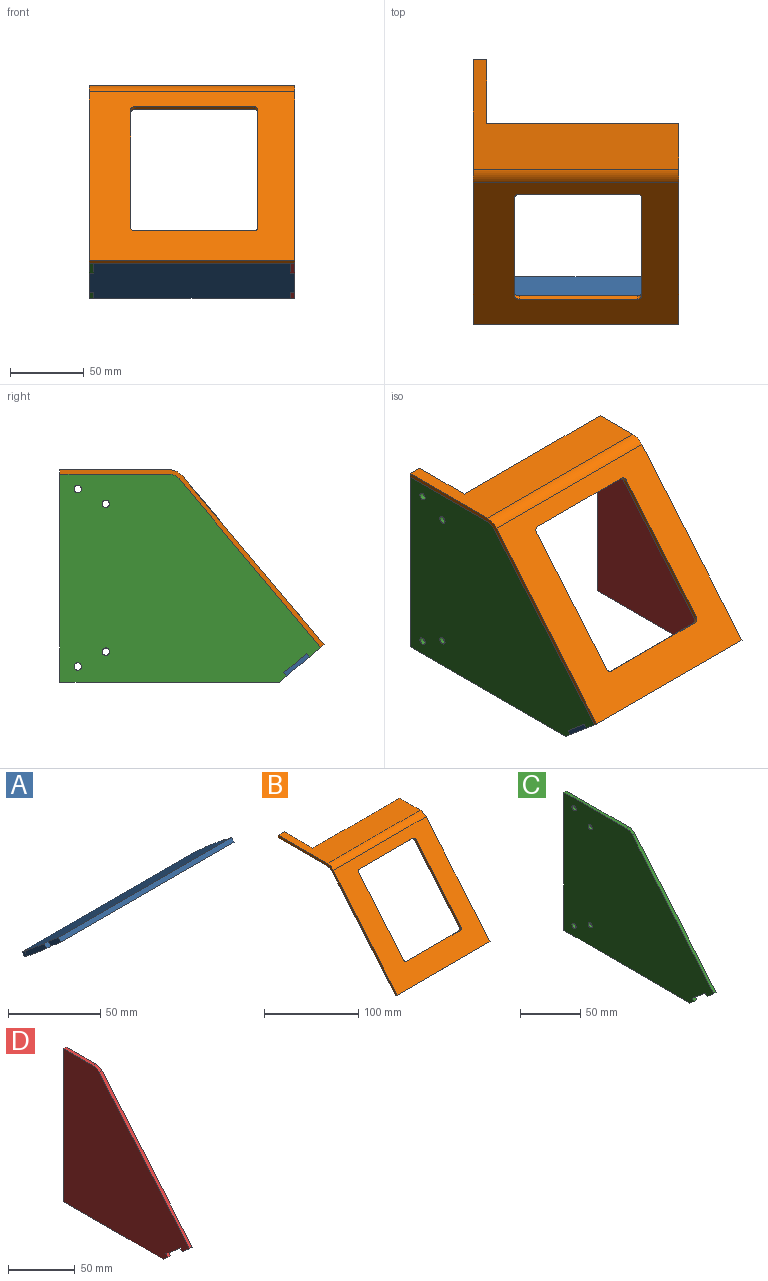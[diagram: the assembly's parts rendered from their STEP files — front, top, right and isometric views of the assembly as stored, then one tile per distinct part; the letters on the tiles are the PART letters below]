
ASSEMBLY  parts=4 mates=3
PART A: 14 faces, bbox 139x29.7x25.6 mm
  f0: plane 17.25x15.15mm, normal (1,0,0), area 60mm2, adj f1,f11,f12,f13
  f1: plane 3x2.3mm, normal (0,-0.77,0.64), area 9mm2, adj f0,f2,f12,f13
  f2: plane 9.59x8.73mm, normal (1,0,0), area 30mm2, adj f1,f3,f12,f13
  f3: plane 133x2.3mm, normal (0,-0.77,0.64), area 399mm2, adj f2,f4,f12,f13
  f4: plane 9.59x8.73mm, normal (-1,0,0), area 30mm2, adj f3,f5,f12,f13
  f5: plane 3x2.3mm, normal (0,-0.77,0.64), area 9mm2, adj f4,f6,f12,f13
  f6: plane 17.25x15.15mm, normal (-1,0,0), area 60mm2, adj f5,f7,f12,f13
  f7: plane 3x2.3mm, normal (0,0.77,-0.64), area 9mm2, adj f6,f8,f12,f13
  f8: plane 6.75x6.35mm, normal (-1,0,0), area 18.9mm2, adj f7,f9,f12,f13
  f9: plane 133x2.3mm, normal (0,0.77,-0.64), area 399mm2, adj f8,f10,f12,f13
  f10: plane 6.75x6.35mm, normal (1,0,0), area 18.9mm2, adj f9,f11,f12,f13
  f11: plane 3x2.3mm, normal (0,0.77,-0.64), area 9mm2, adj f0,f10,f12,f13
  f12: plane 139x27.81mm, normal (0,0.64,0.77), area 4947.9mm2, adj f0,f1,f2,f3,f4,f5,f6,f7
  f13: plane 139x27.81mm, normal (0,-0.64,-0.77), area 4947.9mm2, adj f0,f1,f2,f3,f4,f5,f6,f7
PART B: 20 faces, bbox 139x178.6x120.2 mm
  f0: plane 130x3mm, normal (0,1,0), area 390mm2, adj f5,f6,f9,f19
  f1: plane 139x114.14mm, normal (0,0.77,-0.64), area 11259.2mm2, adj f3,f4,f8,f9,f10,f11,f12,f13
  f2: plane 139x114.14mm, normal (0,-0.77,0.64), area 11259.2mm2, adj f3,f7,f8,f9,f10,f11,f12,f13
  f3: plane 139x2.3mm, normal (0,-0.64,-0.77), area 417mm2, adj f1,f2,f8,f9
  f4: cylinder r=8.57mm len=139mm, axis (1,0,0), area 1039.5mm2, adj f1,f5,f8,f9
  f5: plane 139x74mm, normal (0,0,-1), area 4696.5mm2, adj f0,f4,f8,f9,f18,f19
  f6: plane 139x74mm, normal (0,0,1), area 4696.5mm2, adj f0,f7,f8,f9,f18,f19
  f7: cylinder r=11.57mm len=139mm, axis (1,0,0), area 1403.4mm2, adj f2,f6,f8,f9
  f8: plane 178.64x120.21mm, normal (-1,0,0), area 695.4mm2, adj f1,f2,f3,f4,f5,f6,f7,f18
  f9: plane 135.64x120.21mm, normal (1,0,0), area 566.4mm2, adj f0,f1,f2,f3,f4,f5,f6,f7
  f10: plane 81.6x69.15mm, normal (-1,0,0), area 312mm2, adj f1,f2,f11,f17
  f11: cylinder r=3mm len=4.23mm, axis (0,-0.77,0.64), area 14.1mm2, adj f1,f2,f10,f12
  f12: plane 80x2.3mm, normal (0,-0.64,-0.77), area 240mm2, adj f1,f2,f11,f13
  f13: cylinder r=3mm len=4.23mm, axis (0,-0.77,0.64), area 14.1mm2, adj f1,f2,f12,f14
  f14: plane 81.6x69.15mm, normal (1,0,0), area 312mm2, adj f1,f2,f13,f15
  f15: cylinder r=3mm len=4.23mm, axis (0,-0.77,0.64), area 14.1mm2, adj f1,f2,f14,f16
  f16: plane 80x2.3mm, normal (0,0.64,0.77), area 240mm2, adj f1,f2,f15,f17
  f17: cylinder r=3mm len=4.23mm, axis (0,-0.77,0.64), area 14.1mm2, adj f1,f2,f10,f16
  f18: plane 9x3mm, normal (0,1,0), area 27mm2, adj f5,f6,f8,f19
  f19: plane 43x3mm, normal (1,0,0), area 129mm2, adj f0,f5,f6,f18
PART C: 16 faces, bbox 3x176.3x140.6 mm
  f0: plane 74x3mm, normal (0,0,1), area 222mm2, adj f1,f12,f14,f15
  f1: cylinder r=8.57mm len=6.57mm, axis (-1,0,0), area 22.4mm2, adj f0,f2,f14,f15
  f2: plane 114.14x95.78mm, normal (0,-0.77,0.64), area 447mm2, adj f1,f3,f14,f15
  f3: plane 7.66x6.43mm, normal (0,-0.64,-0.77), area 30mm2, adj f2,f4,f14,f15
  f4: plane 3x2.3mm, normal (0,0.77,-0.64), area 9mm2, adj f3,f5,f14,f15
  f5: plane 15.32x12.86mm, normal (0,-0.64,-0.77), area 60mm2, adj f4,f6,f14,f15
  f6: plane 3x2.3mm, normal (0,-0.77,0.64), area 9mm2, adj f5,f7,f14,f15
  f7: plane 4.92x4.13mm, normal (0,-0.64,-0.77), area 19.3mm2, adj f6,f8,f14,f15
  f8: plane 148.44x3mm, normal (0,0,-1), area 445.3mm2, adj f7,f12,f14,f15
  f9: cylinder r=2.5mm len=5mm, axis (-1,0,0), area 47.1mm2, adj f14,f15
  f10: cylinder r=2.5mm len=5mm, axis (-1,0,0), area 47.1mm2, adj f14,f15
  f11: cylinder r=2.5mm len=5mm, axis (-1,0,0), area 47.1mm2, adj f14,f15
  f12: plane 140.62x3mm, normal (0,1,0), area 421.9mm2, adj f0,f8,f14,f15
  f13: cylinder r=2.5mm len=5mm, axis (-1,0,0), area 47.1mm2, adj f14,f15
  f14: plane 176.35x140.62mm, normal (1,0,0), area 18566.8mm2, adj f0,f1,f2,f3,f4,f5,f6,f7
  f15: plane 176.35x140.62mm, normal (-1,0,0), area 18566.8mm2, adj f0,f1,f2,f3,f4,f5,f6,f7
PART D: 12 faces, bbox 3x133.3x140.6 mm
  f0: plane 140.62x3mm, normal (0,1,0), area 421.9mm2, adj f1,f9,f10,f11
  f1: plane 31x3mm, normal (0,0,1), area 93mm2, adj f0,f2,f10,f11
  f2: cylinder r=8.57mm len=6.57mm, axis (1,0,0), area 22.4mm2, adj f1,f3,f10,f11
  f3: plane 114.14x95.78mm, normal (0,-0.77,0.64), area 447mm2, adj f2,f4,f10,f11
  f4: plane 7.66x6.43mm, normal (0,-0.64,-0.77), area 30mm2, adj f3,f5,f10,f11
  f5: plane 3x2.3mm, normal (0,0.77,-0.64), area 9mm2, adj f4,f6,f10,f11
  f6: plane 15.32x12.86mm, normal (0,-0.64,-0.77), area 60mm2, adj f5,f7,f10,f11
  f7: plane 3x2.3mm, normal (0,-0.77,0.64), area 9mm2, adj f6,f8,f10,f11
  f8: plane 4.92x4.13mm, normal (0,-0.64,-0.77), area 19.3mm2, adj f7,f9,f10,f11
  f9: plane 105.44x3mm, normal (0,0,-1), area 316.3mm2, adj f0,f8,f10,f11
  f10: plane 140.62x133.35mm, normal (-1,0,0), area 12598.7mm2, adj f0,f1,f2,f3,f4,f5,f6,f7
  f11: plane 140.62x133.35mm, normal (1,0,0), area 12598.7mm2, adj f0,f1,f2,f3,f4,f5,f6,f7
PLACE A t=(87.94,-8.15,8.84)mm
PLACE B t=(87.94,-8.15,8.84)mm
PLACE C t=(-48.06,-8.15,8.84)mm fixed
PLACE D t=(223.94,-8.15,8.84)mm
MATE fastened A.f12 <-> D.f6  axis (0,0.64,0.77) through (93.94,-87.51,-26.69)mm
MATE fastened B.f1 <-> C.f2  axis (0,0.77,-0.64) through (-45.06,-97.1,-22.56)mm
MATE fastened A.f12 <-> C.f5  axis (0,0.64,0.77) through (-45.06,-87.51,-26.69)mm
